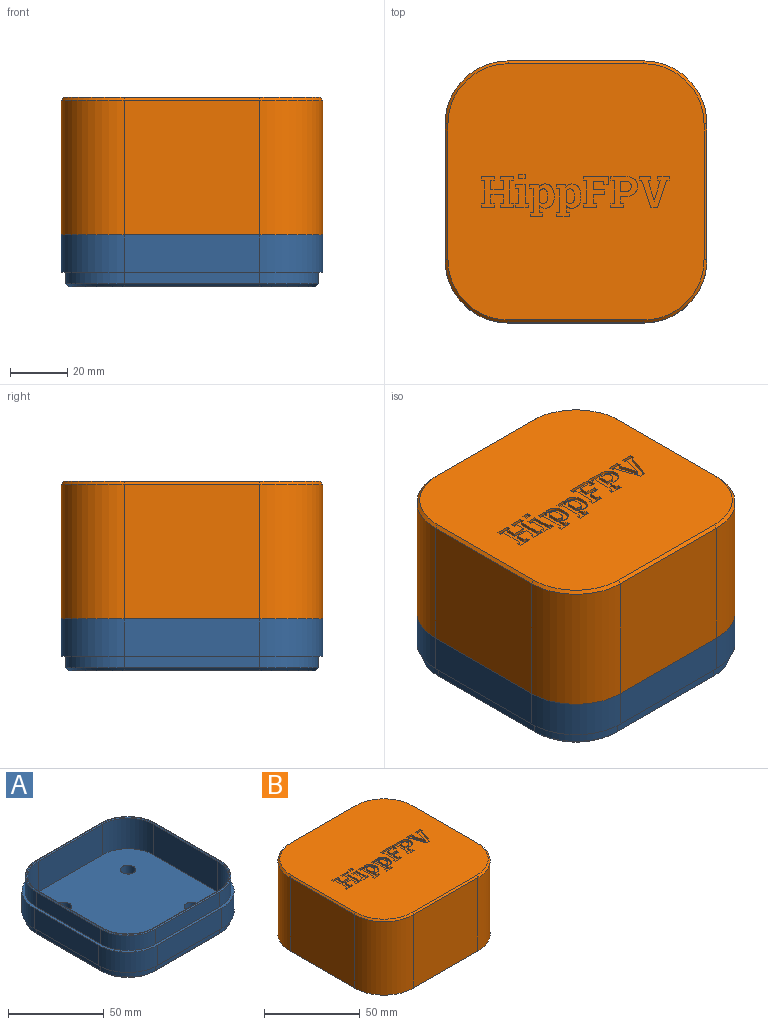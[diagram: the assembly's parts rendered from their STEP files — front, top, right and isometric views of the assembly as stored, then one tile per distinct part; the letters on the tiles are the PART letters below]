
ASSEMBLY  parts=2 mates=1
PART A: 69 faces, bbox 91.4x91.4x28 mm
  f0: plane 47.38x13mm, normal (-1,0,0), area 615.9mm2, adj f4,f7,f34,f43
  f1: plane 47.38x13mm, normal (0,1,0), area 615.9mm2, adj f4,f5,f34,f43
  f2: plane 47.38x13mm, normal (1,0,0), area 615.9mm2, adj f5,f6,f34,f43
  f3: plane 47.38x13mm, normal (0,-1,0), area 615.9mm2, adj f6,f7,f34,f43
  f4: cylinder r=22mm len=22mm, axis (0,0,1), area 449.2mm2, adj f0,f1,f34,f43
  f5: cylinder r=22mm len=22mm, axis (0,0,1), area 449.2mm2, adj f1,f2,f34,f43
  f6: cylinder r=22mm len=22mm, axis (0,0,1), area 449.2mm2, adj f2,f3,f34,f43
  f7: cylinder r=22mm len=22mm, axis (0,0,1), area 449.2mm2, adj f0,f3,f34,f43
  f8: plane 87.18x87.18mm, normal (0,0,1), area 125.3mm2, adj f53,f54,f55,f56,f57,f58,f59,f60
  f9: plane 47.38x19.5mm, normal (0,-1,0), area 923.8mm2, adj f10,f16,f17,f68
  f10: cylinder r=19mm len=19.5mm, axis (0,0,-1), area 582mm2, adj f9,f11,f17,f66
  f11: plane 47.38x19.5mm, normal (-1,0,0), area 923.8mm2, adj f10,f12,f17,f64
  f12: cylinder r=19mm len=19.5mm, axis (0,0,-1), area 582mm2, adj f11,f13,f17,f62
  f13: plane 47.38x19.5mm, normal (0,1,0), area 923.8mm2, adj f12,f14,f17,f61
  f14: cylinder r=19mm len=19.5mm, axis (0,0,-1), area 582mm2, adj f13,f15,f17,f63
  f15: plane 47.38x19.5mm, normal (1,0,0), area 923.8mm2, adj f14,f16,f17,f65
  f16: cylinder r=19mm len=19.5mm, axis (0,0,-1), area 582mm2, adj f9,f15,f17,f67
  f17: plane 85.38x85.38mm, normal (0,0,1), area 6778.1mm2, adj f9,f10,f11,f12,f13,f14,f15,f16
  f18: cylinder r=4mm len=8mm, axis (0,0,1), area 125.7mm2, adj f17,f19
  f19: plane 8x8mm, normal (0,0,1), area 50.3mm2, adj f18
  f20: cylinder r=4mm len=8mm, axis (0,0,1), area 125.7mm2, adj f17,f21
  f21: plane 8x8mm, normal (0,0,1), area 50.3mm2, adj f20
  f22: cylinder r=4mm len=8mm, axis (0,0,1), area 125.7mm2, adj f17,f23
  f23: plane 8x8mm, normal (0,0,1), area 50.3mm2, adj f22
  f24: cylinder r=4mm len=8mm, axis (0,0,1), area 125.7mm2, adj f17,f25
  f25: plane 8x8mm, normal (0,0,1), area 50.3mm2, adj f24
  f26: cylinder r=20.4mm len=20.4mm, axis (0,0,1), area 304.4mm2, adj f27,f33,f34,f60
  f27: plane 47.38x9.5mm, normal (1,0,0), area 450.1mm2, adj f26,f28,f34,f58
  f28: cylinder r=20.4mm len=20.4mm, axis (0,0,1), area 304.4mm2, adj f27,f29,f34,f56
  f29: plane 47.38x9.5mm, normal (0,-1,0), area 450.1mm2, adj f28,f30,f34,f54
  f30: cylinder r=20.4mm len=20.4mm, axis (0,0,1), area 304.4mm2, adj f29,f31,f34,f53
  f31: plane 47.38x9.5mm, normal (-1,0,0), area 450.1mm2, adj f30,f32,f34,f55
  f32: cylinder r=20.4mm len=20.4mm, axis (0,0,1), area 304.4mm2, adj f31,f33,f34,f57
  f33: plane 47.38x9.5mm, normal (0,1,0), area 450.1mm2, adj f26,f32,f34,f59
  f34: plane 91.38x91.38mm, normal (0,0,1), area 516.3mm2, adj f0,f1,f2,f3,f4,f5,f6,f7
  f35: plane 47.38x4mm, normal (1,0,0), area 189.5mm2, adj f36,f42,f43,f50
  f36: cylinder r=20.4mm len=20.4mm, axis (0,0,-1), area 128.2mm2, adj f35,f37,f43,f52
  f37: plane 47.38x4mm, normal (0,1,0), area 189.5mm2, adj f36,f38,f43,f51
  f38: cylinder r=20.4mm len=20.4mm, axis (0,0,-1), area 128.2mm2, adj f37,f39,f43,f49
  f39: plane 47.38x4mm, normal (-1,0,0), area 189.5mm2, adj f38,f40,f43,f47
  f40: cylinder r=20.4mm len=20.4mm, axis (0,0,-1), area 128.2mm2, adj f39,f41,f43,f45
  f41: plane 47.38x4mm, normal (0,-1,0), area 189.5mm2, adj f40,f42,f43,f46
  f42: cylinder r=20.4mm len=20.4mm, axis (0,0,-1), area 128.2mm2, adj f35,f41,f43,f48
  f43: plane 91.38x91.38mm, normal (0,0,-1), area 516.3mm2, adj f0,f1,f2,f3,f4,f5,f6,f7
  f44: plane 86.18x86.18mm, normal (0,0,-1), area 7103.3mm2, adj f45,f46,f47,f48,f49,f50,f51,f52
  f45: cone r=20.4mm half-angle=45deg, axis (0,0,1), area 44.2mm2, adj f40,f44,f46,f47
  f46: plane 47.38x1mm, normal (0,-0.71,-0.71), area 67mm2, adj f41,f44,f45,f48
  f47: plane 47.38x1mm, normal (-0.71,0,-0.71), area 67mm2, adj f39,f44,f45,f49
  f48: cone r=20.4mm half-angle=45deg, axis (0,0,1), area 44.2mm2, adj f42,f44,f46,f50
  f49: cone r=20.4mm half-angle=45deg, axis (0,0,1), area 44.2mm2, adj f38,f44,f47,f51
  f50: plane 47.38x1mm, normal (0.71,0,-0.71), area 67mm2, adj f35,f44,f48,f52
  f51: plane 47.38x1mm, normal (0,0.71,-0.71), area 67mm2, adj f37,f44,f49,f52
  f52: cone r=20.4mm half-angle=45deg, axis (0,0,1), area 44.2mm2, adj f36,f44,f50,f51
  f53: cone r=19.9mm half-angle=45deg, axis (0,0,-1), area 22.4mm2, adj f8,f30,f54,f55
  f54: plane 47.38x0.5mm, normal (0,-0.71,0.71), area 33.5mm2, adj f8,f29,f53,f56
  f55: plane 47.38x0.5mm, normal (-0.71,0,0.71), area 33.5mm2, adj f8,f31,f53,f57
  f56: cone r=19.9mm half-angle=45deg, axis (0,0,-1), area 22.4mm2, adj f8,f28,f54,f58
  f57: cone r=19.9mm half-angle=45deg, axis (0,0,-1), area 22.4mm2, adj f8,f32,f55,f59
  f58: plane 47.38x0.5mm, normal (0.71,0,0.71), area 33.5mm2, adj f8,f27,f56,f60
  f59: plane 47.38x0.5mm, normal (0,0.71,0.71), area 33.5mm2, adj f8,f33,f57,f60
  f60: cone r=19.9mm half-angle=45deg, axis (0,0,-1), area 22.4mm2, adj f8,f26,f58,f59
  f61: plane 47.38x0.5mm, normal (0,0.71,0.71), area 33.5mm2, adj f8,f13,f62,f63
  f62: cone r=19mm half-angle=45deg, axis (0,0,1), area 21.4mm2, adj f8,f12,f61,f64
  f63: cone r=19mm half-angle=45deg, axis (0,0,1), area 21.4mm2, adj f8,f14,f61,f65
  f64: plane 47.38x0.5mm, normal (-0.71,0,0.71), area 33.5mm2, adj f8,f11,f62,f66
  f65: plane 47.38x0.5mm, normal (0.71,0,0.71), area 33.5mm2, adj f8,f15,f63,f67
  f66: cone r=19mm half-angle=45deg, axis (0,0,1), area 21.4mm2, adj f8,f10,f64,f68
  f67: cone r=19mm half-angle=45deg, axis (0,0,1), area 21.4mm2, adj f8,f16,f65,f68
  f68: plane 47.38x0.5mm, normal (0,-0.71,0.71), area 33.5mm2, adj f8,f9,f66,f67
PART B: 207 faces, bbox 91.4x91.4x48 mm
  f0: plane 89.38x89.38mm, normal (0,0,1), area 7218.9mm2, adj f28,f29,f30,f31,f32,f33,f34,f35
  f1: plane 91.38x91.38mm, normal (0,0,-1), area 484.5mm2, adj f2,f3,f4,f5,f6,f7,f8,f9
  f2: cylinder r=22mm len=47mm, axis (0,0,-1), area 1624.2mm2, adj f1,f3,f9,f33
  f3: plane 47.38x47mm, normal (0,-1,0), area 2226.7mm2, adj f1,f2,f4,f35
  f4: cylinder r=22mm len=47mm, axis (0,0,-1), area 1624.2mm2, adj f1,f3,f5,f34
  f5: plane 47.38x47mm, normal (1,0,0), area 2226.7mm2, adj f1,f4,f6,f32
  f6: cylinder r=22mm len=47mm, axis (0,0,-1), area 1624.2mm2, adj f1,f5,f7,f30
  f7: plane 47.38x47mm, normal (0,1,0), area 2226.7mm2, adj f1,f6,f8,f28
  f8: cylinder r=22mm len=47mm, axis (0,0,-1), area 1624.2mm2, adj f1,f7,f9,f29
  f9: plane 47.38x47mm, normal (-1,0,0), area 2226.7mm2, adj f1,f2,f8,f31
  f10: cylinder r=20.5mm len=20.5mm, axis (0,0,-1), area 338.1mm2, adj f1,f11,f17,f18
  f11: plane 47.38x10.5mm, normal (0,-1,0), area 497.4mm2, adj f1,f10,f12,f18
  f12: cylinder r=20.5mm len=20.5mm, axis (0,0,-1), area 338.1mm2, adj f1,f11,f13,f18
  f13: plane 47.38x10.5mm, normal (-1,0,0), area 497.4mm2, adj f1,f12,f14,f18
  f14: cylinder r=20.5mm len=20.5mm, axis (0,0,-1), area 338.1mm2, adj f1,f13,f15,f18
  f15: plane 47.38x10.5mm, normal (0,1,0), area 497.4mm2, adj f1,f14,f16,f18
  f16: cylinder r=20.5mm len=20.5mm, axis (0,0,-1), area 338.1mm2, adj f1,f15,f17,f18
  f17: plane 47.38x10.5mm, normal (1,0,0), area 497.4mm2, adj f1,f10,f16,f18
  f18: plane 88.38x88.38mm, normal (0,0,-1), area 470.4mm2, adj f10,f11,f12,f13,f14,f15,f16,f17
  f19: plane 85.38x85.38mm, normal (0,0,-1), area 6979.2mm2, adj f20,f21,f22,f23,f24,f25,f26,f27
  f20: plane 47.38x34.5mm, normal (-1,0,0), area 1634.5mm2, adj f18,f19,f21,f27
  f21: cylinder r=19mm len=34.5mm, axis (0,0,-1), area 1029.7mm2, adj f18,f19,f20,f22
  f22: plane 47.38x34.5mm, normal (0,1,0), area 1634.5mm2, adj f18,f19,f21,f23
  f23: cylinder r=19mm len=34.5mm, axis (0,0,-1), area 1029.7mm2, adj f18,f19,f22,f24
  f24: plane 47.38x34.5mm, normal (1,0,0), area 1634.5mm2, adj f18,f19,f23,f25
  f25: cylinder r=19mm len=34.5mm, axis (0,0,-1), area 1029.7mm2, adj f18,f19,f24,f26
  f26: plane 47.38x34.5mm, normal (0,-1,0), area 1634.5mm2, adj f18,f19,f25,f27
  f27: cylinder r=19mm len=34.5mm, axis (0,0,-1), area 1029.7mm2, adj f18,f19,f20,f26
  f28: plane 47.38x1mm, normal (0,0.71,0.71), area 67mm2, adj f0,f7,f29,f30
  f29: cone r=21mm half-angle=45deg, axis (0,0,-1), area 47.8mm2, adj f0,f8,f28,f31
  f30: cone r=21mm half-angle=45deg, axis (0,0,-1), area 47.8mm2, adj f0,f6,f28,f32
  f31: plane 47.38x1mm, normal (-0.71,0,0.71), area 67mm2, adj f0,f9,f29,f33
  f32: plane 47.38x1mm, normal (0.71,0,0.71), area 67mm2, adj f0,f5,f30,f34
  f33: cone r=21mm half-angle=45deg, axis (0,0,-1), area 47.8mm2, adj f0,f2,f31,f35
  f34: cone r=21mm half-angle=45deg, axis (0,0,-1), area 47.8mm2, adj f0,f4,f32,f35
  f35: plane 47.38x1mm, normal (0,-0.71,0.71), area 67mm2, adj f0,f3,f33,f34
  f36: plane 1.32x1mm, normal (1,0,0), area 1.3mm2, adj f0,f37,f45,f46
  f37: plane 4.32x1mm, normal (0,1,0), area 4.3mm2, adj f0,f36,f38,f46
  f38: plane 1.32x1mm, normal (-1,0,0), area 1.3mm2, adj f0,f37,f39,f46
  f39: plane 1.05x1mm, normal (-0.21,-0.98,0), area 1.1mm2, adj f0,f38,f40,f46
  f40: plane 6.61x1mm, normal (-1,0,0), area 6.6mm2, adj f0,f39,f41,f46
  f41: plane 3.38x1mm, normal (0,-1,0), area 3.4mm2, adj f0,f40,f42,f46
  f42: plane 1.33x1mm, normal (1,0,0), area 1.3mm2, adj f0,f41,f43,f46
  f43: plane 1.17x1mm, normal (0.19,0.98,0), area 1.2mm2, adj f0,f42,f44,f46
  f44: plane 5.06x1mm, normal (1,0,0), area 5.1mm2, adj f0,f43,f45,f46
  f45: plane 1.06x1mm, normal (0.21,-0.98,0), area 1.1mm2, adj f0,f36,f44,f46
  f46: plane 8.15x4.43mm, normal (0,0,1), area 22.7mm2, adj f36,f37,f38,f39,f40,f41,f42,f43
  f47: plane 1.65x1mm, normal (-1,0,0), area 1.6mm2, adj f0,f48,f50,f51
  f48: plane 2.2x1mm, normal (0,-1,0), area 2.2mm2, adj f0,f47,f49,f51
  f49: plane 1.65x1mm, normal (1,0,0), area 1.6mm2, adj f0,f48,f50,f51
  f50: plane 2.2x1mm, normal (0,1,0), area 2.2mm2, adj f0,f47,f49,f51
  f51: plane 2.2x1.65mm, normal (0,0,1), area 3.6mm2, adj f47,f48,f49,f50
  f52: plane 1.32x1mm, normal (1,0,0), area 1.3mm2, adj f0,f53,f69,f70
  f53: plane 4.54x1mm, normal (0,1,0), area 4.5mm2, adj f0,f52,f54,f70
  f54: plane 1.32x1mm, normal (-1,0,0), area 1.3mm2, adj f0,f53,f55,f70
  f55: plane 1.17x1mm, normal (-0.19,-0.98,0), area 1.2mm2, adj f0,f54,f56,f70
  f56: plane 3.01x1mm, normal (-1,0,0), area 3mm2, adj f0,f55,f57,f70
  f57: plane 3.84x1mm, normal (0,1,0), area 3.8mm2, adj f0,f56,f58,f70
  f58: plane 1.7x1mm, normal (-1,0,0), area 1.7mm2, adj f0,f57,f59,f70
  f59: plane 3.84x1mm, normal (0,-1,0), area 3.8mm2, adj f0,f58,f60,f70
  f60: plane 3.02x1mm, normal (-1,0,0), area 3mm2, adj f0,f59,f61,f70
  f61: plane 3.58x1mm, normal (0,1,0), area 3.6mm2, adj f0,f60,f62,f70
  f62: plane 1.31x1mm, normal (1,0.08,0), area 1.3mm2, adj f0,f61,f63,f70
  f63: plane 1.69x1mm, normal (0,1,0), area 1.7mm2, adj f0,f62,f64,f70
  f64: plane 3.01x1mm, normal (-1,0,0), area 3mm2, adj f0,f63,f65,f70
  f65: plane 8.73x1mm, normal (0,-1,0), area 8.7mm2, adj f0,f64,f66,f70
  f66: plane 1.33x1mm, normal (1,0,0), area 1.3mm2, adj f0,f65,f67,f70
  f67: plane 1.17x1mm, normal (0.19,0.98,0), area 1.2mm2, adj f0,f66,f68,f70
  f68: plane 7.87x1mm, normal (1,0,0), area 7.9mm2, adj f0,f67,f69,f70
  f69: plane 1.17x1mm, normal (0.19,-0.98,0), area 1.2mm2, adj f0,f52,f68,f70
  f70: plane 10.97x8.73mm, normal (0,0,1), area 47.1mm2, adj f52,f53,f54,f55,f56,f57,f58,f59
  f71: plane 1.33x1mm, normal (-1,0,0), area 1.3mm2, adj f0,f72,f88,f89
  f72: plane 4.01x1mm, normal (0,-1,0), area 4mm2, adj f0,f71,f73,f89
  f73: plane 1.33x1mm, normal (1,0,0), area 1.3mm2, adj f0,f72,f74,f89
  f74: plane 1x0.9mm, normal (0.13,0.99,0), area 0.9mm2, adj f0,f73,f75,f89
  f75: plane 9.52x3.24mm, normal (0.95,0.32,0), area 10.1mm2, adj f0,f74,f76,f89
  f76: plane 2.26x1mm, normal (0,1,0), area 2.3mm2, adj f0,f75,f77,f89
  f77: plane 9.52x3.23mm, normal (-0.95,0.32,0), area 10.1mm2, adj f0,f76,f78,f89
  f78: plane 1x0.92mm, normal (-0.13,0.99,0), area 0.9mm2, adj f0,f77,f79,f89
  f79: plane 1.33x1mm, normal (-1,0,0), area 1.3mm2, adj f0,f78,f80,f89
  f80: plane 4.01x1mm, normal (0,-1,0), area 4mm2, adj f0,f79,f81,f89
  f81: plane 1.33x1mm, normal (1,0,0), area 1.3mm2, adj f0,f80,f82,f89
  f82: plane 1x0.83mm, normal (0.18,0.98,0), area 0.8mm2, adj f0,f81,f83,f89
  f83: plane 6.6x1.95mm, normal (0.96,-0.28,0), area 6.9mm2, adj f0,f82,f84,f89
  f84: plane 1x0.59mm, normal (0.98,-0.21,0), area 0.6mm2, adj f0,f83,f85,f89
  f85: plane 1x0.05mm, normal (0,-1,0), area 0mm2, adj f0,f84,f86,f89
  f86: plane 1x0.6mm, normal (-0.98,-0.22,0), area 0.6mm2, adj f0,f85,f87,f89
  f87: plane 6.58x1.94mm, normal (-0.96,-0.28,0), area 6.9mm2, adj f0,f86,f88,f89
  f88: plane 1x0.84mm, normal (-0.18,0.98,0), area 0.8mm2, adj f0,f71,f87,f89
  f89: plane 10.97x10.56mm, normal (0,0,1), area 48.7mm2, adj f71,f72,f73,f74,f75,f76,f77,f78
  f90: plane 1.18x1mm, normal (0.19,0.98,0), area 1.2mm2, adj f0,f91,f119,f120
  f91: plane 8.18x1mm, normal (1,0,0), area 8.2mm2, adj f0,f90,f92,f120
  f92: plane 1.06x1mm, normal (0.21,-0.98,0), area 1.1mm2, adj f0,f91,f93,f120
  f93: plane 1.33x1mm, normal (1,0,0), area 1.3mm2, adj f0,f92,f94,f120
  f94: plane 4.32x1mm, normal (0,1,0), area 4.3mm2, adj f0,f93,f95,f120
  f95: plane 1.33x1mm, normal (-1,0,0), area 1.3mm2, adj f0,f94,f96,f120
  f96: plane 1.06x1mm, normal (-0.21,-0.98,0), area 1.1mm2, adj f0,f95,f97,f120
  f97: plane 2.36x1mm, normal (-1,0,0), area 2.4mm2, adj f0,f96,f98,f120
  f98: extruded ~1x0.85mm, area 1.1mm2, adj f0,f97,f99,f120
  f99: extruded ~1.14x1mm, area 1.2mm2, adj f0,f98,f100,f120
  f100: extruded ~2.34x1.1mm, area 2.7mm2, adj f0,f99,f101,f120
  f101: extruded ~2.91x1mm, area 3.1mm2, adj f0,f100,f102,f120
  f102: plane 1x0.16mm, normal (-1,0,0), area 0.2mm2, adj f0,f101,f103,f120
  f103: extruded ~3.11x1mm, area 3.3mm2, adj f0,f102,f104,f120
  f104: extruded ~2.35x1.18mm, area 2.7mm2, adj f0,f103,f105,f120
  f105: extruded ~1.18x1mm, area 1.2mm2, adj f0,f104,f106,f120
  f106: extruded ~1x0.87mm, area 1.2mm2, adj f0,f105,f107,f120
  f107: plane 1x0.95mm, normal (-0.99,-0.11,0), area 1mm2, adj f0,f106,f108,f120
  f108: plane 3.2x1mm, normal (0,-1,0), area 3.2mm2, adj f0,f107,f119,f120
  f109: plane 1x0.16mm, normal (1,0,0), area 0.2mm2, adj f110,f118,f120,f121
  f110: extruded ~1.7x1mm, area 1.8mm2, adj f109,f111,f120,f121
  f111: extruded ~1.17x1mm, area 1.4mm2, adj f110,f112,f120,f121
  f112: extruded ~1x0.86mm, area 0.9mm2, adj f111,f113,f120,f121
  f113: extruded ~1x0.55mm, area 0.8mm2, adj f112,f114,f120,f121
  f114: plane 3.57x1mm, normal (-1,0,0), area 3.6mm2, adj f113,f115,f120,f121
  f115: extruded ~1x0.58mm, area 0.8mm2, adj f114,f116,f120,f121
  f116: extruded ~1x0.85mm, area 0.9mm2, adj f115,f117,f120,f121
  f117: extruded ~1.18x1mm, area 1.5mm2, adj f116,f118,f120,f121
  f118: extruded ~1.87x1mm, area 1.9mm2, adj f109,f117,f120,f121
  f119: plane 1.33x1mm, normal (1,0,0), area 1.3mm2, adj f0,f90,f108,f120
  f120: plane 11.44x8.53mm, normal (0,0,1), area 53.9mm2, adj f90,f91,f92,f93,f94,f95,f96,f97
  f121: plane 5.06x2.96mm, normal (0,0,1), area 13.1mm2, adj f109,f110,f111,f112,f113,f114,f115,f116
  f122: plane 1.18x1mm, normal (0.19,0.98,0), area 1.2mm2, adj f0,f123,f151,f152
  f123: plane 8.18x1mm, normal (1,0,0), area 8.2mm2, adj f0,f122,f124,f152
  f124: plane 1.06x1mm, normal (0.21,-0.98,0), area 1.1mm2, adj f0,f123,f125,f152
  f125: plane 1.33x1mm, normal (1,0,0), area 1.3mm2, adj f0,f124,f126,f152
  f126: plane 4.32x1mm, normal (0,1,0), area 4.3mm2, adj f0,f125,f127,f152
  f127: plane 1.33x1mm, normal (-1,0,0), area 1.3mm2, adj f0,f126,f128,f152
  f128: plane 1.06x1mm, normal (-0.21,-0.98,0), area 1.1mm2, adj f0,f127,f129,f152
  f129: plane 2.36x1mm, normal (-1,0,0), area 2.4mm2, adj f0,f128,f130,f152
  f130: extruded ~1x0.85mm, area 1.1mm2, adj f0,f129,f131,f152
  f131: extruded ~1.14x1mm, area 1.2mm2, adj f0,f130,f132,f152
  f132: extruded ~2.34x1.1mm, area 2.7mm2, adj f0,f131,f133,f152
  f133: extruded ~2.91x1mm, area 3.1mm2, adj f0,f132,f134,f152
  f134: plane 1x0.16mm, normal (-1,0,0), area 0.2mm2, adj f0,f133,f135,f152
  f135: extruded ~3.11x1mm, area 3.3mm2, adj f0,f134,f136,f152
  f136: extruded ~2.35x1.18mm, area 2.7mm2, adj f0,f135,f137,f152
  f137: extruded ~1.18x1mm, area 1.2mm2, adj f0,f136,f138,f152
  f138: extruded ~1x0.87mm, area 1.2mm2, adj f0,f137,f139,f152
  f139: plane 1x0.95mm, normal (-0.99,-0.11,0), area 1mm2, adj f0,f138,f140,f152
  f140: plane 3.2x1mm, normal (0,-1,0), area 3.2mm2, adj f0,f139,f151,f152
  f141: plane 1x0.16mm, normal (1,0,0), area 0.2mm2, adj f142,f150,f152,f153
  f142: extruded ~1.7x1mm, area 1.8mm2, adj f141,f143,f152,f153
  f143: extruded ~1.17x1mm, area 1.4mm2, adj f142,f144,f152,f153
  f144: extruded ~1x0.86mm, area 0.9mm2, adj f143,f145,f152,f153
  f145: extruded ~1x0.55mm, area 0.8mm2, adj f144,f146,f152,f153
  f146: plane 3.57x1mm, normal (-1,0,0), area 3.6mm2, adj f145,f147,f152,f153
  f147: extruded ~1x0.58mm, area 0.8mm2, adj f146,f148,f152,f153
  f148: extruded ~1x0.85mm, area 0.9mm2, adj f147,f149,f152,f153
  f149: extruded ~1.18x1mm, area 1.5mm2, adj f148,f150,f152,f153
  f150: extruded ~1.87x1mm, area 1.9mm2, adj f141,f149,f152,f153
  f151: plane 1.33x1mm, normal (1,0,0), area 1.3mm2, adj f0,f122,f140,f152
  f152: plane 11.44x8.53mm, normal (0,0,1), area 53.9mm2, adj f122,f123,f124,f125,f126,f127,f128,f129
  f153: plane 5.06x2.96mm, normal (0,0,1), area 13.1mm2, adj f141,f142,f143,f144,f145,f146,f147,f148
  f154: plane 5.22x1mm, normal (0,-1,0), area 5.2mm2, adj f0,f155,f175,f176
  f155: plane 1.33x1mm, normal (1,0,0), area 1.3mm2, adj f0,f154,f156,f176
  f156: plane 1.17x1mm, normal (0.19,0.98,0), area 1.2mm2, adj f0,f155,f157,f176
  f157: plane 7.87x1mm, normal (1,0,0), area 7.9mm2, adj f0,f156,f158,f176
  f158: plane 1.17x1mm, normal (0.19,-0.98,0), area 1.2mm2, adj f0,f157,f159,f176
  f159: plane 1.32x1mm, normal (1,0,0), area 1.3mm2, adj f0,f158,f160,f176
  f160: plane 4.54x1mm, normal (0,1,0), area 4.5mm2, adj f0,f159,f161,f176
  f161: plane 1.32x1mm, normal (-1,0,0), area 1.3mm2, adj f0,f160,f162,f176
  f162: plane 1.17x1mm, normal (-0.19,-0.98,0), area 1.2mm2, adj f0,f161,f163,f176
  f163: plane 2.43x1mm, normal (-1,0,0), area 2.4mm2, adj f0,f162,f164,f176
  f164: plane 1.85x1mm, normal (0,1,0), area 1.9mm2, adj f0,f163,f165,f176
  f165: extruded ~2.97x1mm, area 3.2mm2, adj f0,f164,f166,f176
  f166: extruded ~2.53x1.09mm, area 2.8mm2, adj f0,f165,f167,f176
  f167: extruded ~2.54x1.09mm, area 2.8mm2, adj f0,f166,f175,f176
  f168: plane 3.6x1mm, normal (-1,0,0), area 3.6mm2, adj f169,f174,f176,f177
  f169: plane 1.85x1mm, normal (0,1,0), area 1.9mm2, adj f168,f170,f176,f177
  f170: extruded ~1.39x1mm, area 1.5mm2, adj f169,f171,f176,f177
  f171: extruded ~1.31x1mm, area 1.4mm2, adj f170,f172,f176,f177
  f172: extruded ~1.28x1mm, area 1.4mm2, adj f171,f173,f176,f177
  f173: extruded ~1.39x1mm, area 1.5mm2, adj f172,f174,f176,f177
  f174: plane 1.85x1mm, normal (0,-1,0), area 1.9mm2, adj f168,f173,f176,f177
  f175: extruded ~2.97x1mm, area 3.2mm2, adj f0,f154,f167,f176
  f176: plane 10.97x9.28mm, normal (0,0,1), area 53mm2, adj f154,f155,f156,f157,f158,f159,f160,f161
  f177: plane 3.72x3.6mm, normal (0,0,1), area 12.1mm2, adj f168,f169,f170,f171,f172,f173,f174
  f178: plane 1.17x1mm, normal (0.19,0.98,0), area 1.2mm2, adj f0,f179,f205,f206
  f179: plane 7.87x1mm, normal (1,0,0), area 7.9mm2, adj f0,f178,f180,f206
  f180: plane 1.17x1mm, normal (0.19,-0.98,0), area 1.2mm2, adj f0,f179,f181,f206
  f181: plane 1.32x1mm, normal (1,0,0), area 1.3mm2, adj f0,f180,f182,f206
  f182: plane 4.54x1mm, normal (0,1,0), area 4.5mm2, adj f0,f181,f183,f206
  f183: plane 1.32x1mm, normal (-1,0,0), area 1.3mm2, adj f0,f182,f184,f206
  f184: plane 1.17x1mm, normal (-0.19,-0.98,0), area 1.2mm2, adj f0,f183,f185,f206
  f185: plane 3.01x1mm, normal (-1,0,0), area 3mm2, adj f0,f184,f186,f206
  f186: plane 4.48x1mm, normal (0,1,0), area 4.5mm2, adj f0,f185,f187,f206
  f187: plane 3.01x1mm, normal (1,0,0), area 3mm2, adj f0,f186,f188,f206
  f188: plane 1.17x1mm, normal (0.19,-0.98,0), area 1.2mm2, adj f0,f187,f189,f206
  f189: plane 1.32x1mm, normal (1,0,0), area 1.3mm2, adj f0,f188,f190,f206
  f190: plane 4.54x1mm, normal (0,1,0), area 4.5mm2, adj f0,f189,f191,f206
  f191: plane 1.32x1mm, normal (-1,0,0), area 1.3mm2, adj f0,f190,f192,f206
  f192: plane 1.17x1mm, normal (-0.19,-0.98,0), area 1.2mm2, adj f0,f191,f193,f206
  f193: plane 7.87x1mm, normal (-1,0,0), area 7.9mm2, adj f0,f192,f194,f206
  f194: plane 1.17x1mm, normal (-0.19,0.98,0), area 1.2mm2, adj f0,f193,f195,f206
  f195: plane 1.33x1mm, normal (-1,0,0), area 1.3mm2, adj f0,f194,f196,f206
  f196: plane 4.54x1mm, normal (0,-1,0), area 4.5mm2, adj f0,f195,f197,f206
  f197: plane 1.33x1mm, normal (1,0,0), area 1.3mm2, adj f0,f196,f198,f206
  f198: plane 1.17x1mm, normal (0.19,0.98,0), area 1.2mm2, adj f0,f197,f199,f206
  f199: plane 3.16x1mm, normal (1,0,0), area 3.2mm2, adj f0,f198,f200,f206
  f200: plane 4.48x1mm, normal (0,-1,0), area 4.5mm2, adj f0,f199,f201,f206
  f201: plane 3.16x1mm, normal (-1,0,0), area 3.2mm2, adj f0,f200,f202,f206
  f202: plane 1.17x1mm, normal (-0.19,0.98,0), area 1.2mm2, adj f0,f201,f203,f206
  f203: plane 1.33x1mm, normal (-1,0,0), area 1.3mm2, adj f0,f202,f204,f206
  f204: plane 4.54x1mm, normal (0,-1,0), area 4.5mm2, adj f0,f203,f205,f206
  f205: plane 1.33x1mm, normal (1,0,0), area 1.3mm2, adj f0,f178,f204,f206
  f206: plane 11.21x10.97mm, normal (0,0,1), area 69.3mm2, adj f178,f179,f180,f181,f182,f183,f184,f185
PLACE A t=(0,0,8)mm
PLACE B t=(0,0,18)mm
MATE fastened A.f3 <-> B.f3  axis (0,-1,0) through (0,-45.69,18)mm
